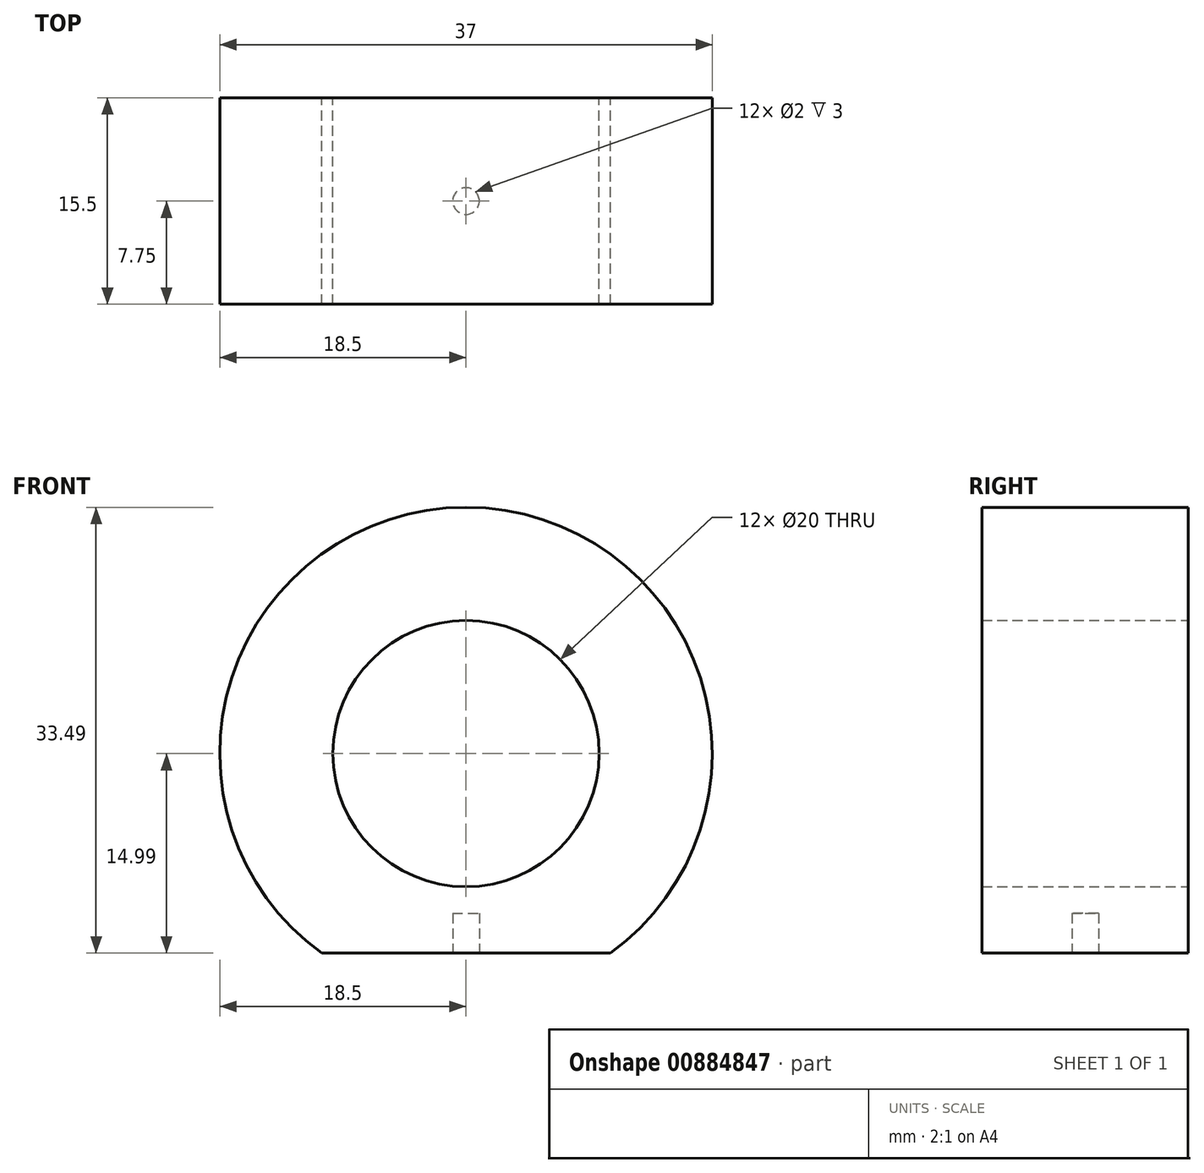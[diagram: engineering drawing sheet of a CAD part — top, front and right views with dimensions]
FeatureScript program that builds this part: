
annotation { "Feature Type Name" : "Feature", "Feature Type Description" : "" }
export const myFeature = defineFeature(function(context is Context, id is Id, definition is map)
    precondition{}
    {
        {
            var Q0;
            Q0=qCreatedBy(makeId("Front.planeOp"),FACE);
            var sketch = newSketch(context, id + "F0", { "sketchPlane" : qUnion([Q0])});
            skArc(sketch, "E0", {"start": v(10.84, -15) * mm, "mid": v(0, 18.5) * mm, "end": v(-10.84, -15) * mm});
            skCircle(sketch, "E1", {"center": v(0, 0) * mm, "radius": 10 * mm});
            skLineSegment(sketch, "E2", {"start": v(-10.84, -15) * mm, "end": v(10.84, -15) * mm});
            skSolve(sketch);
        }
        {
            var Q0;
            Q0=makeQuery(id+"F0.imprint","IMPRINT",FACE,{"disambiguationData":[TD([[makeQuery(id+"F0.imprint","IMPRINT",EDGE,{"derivedFrom":sQuery(id+"F0.wireOp",EDGE,"E0")}),1.0]])]});
            extrude(context, id + "F1", {"entities" : qUnion([Q0]), "depth" : 15.5 * mm, "offsetDistance" : 25 * mm});
        }
        {
            var Q0;
            Q0=makeQuery(id+"F1.opExtrude","SWEPT_FACE",FACE,{"disambiguationData":[OSD([sQuery(id+"F0.wireOp",EDGE,"E2")])]});
            var sketch = newSketch(context, id + "F2", { "sketchPlane" : qUnion([Q0])});
            skCircle(sketch, "E3", {"center": v(0, 7.75) * mm, "radius": 1 * mm});
            skLineSegment(sketch, "E4", {"start": v(10.84, 7.75) * mm, "end": v(-10.84, 7.75) * mm, "construction": true});
            skLineSegment(sketch, "E5", {"start": v(-10.84, 7.75) * mm, "end": v(-11.45, 6.74) * mm, "construction": true});
            skSolve(sketch);
        }
        {
            var Q0;
            Q0 = qSketchRegion(id + "F2", true);
            extrude(context, id + "F3", {"entities" : qUnion([Q0]), "operationType" : NewBodyOperationType.REMOVE, "oppositeDirection" : true, "depth" : 3 * mm, "offsetDistance" : 25 * mm});
        }
    });
